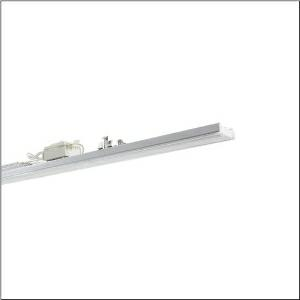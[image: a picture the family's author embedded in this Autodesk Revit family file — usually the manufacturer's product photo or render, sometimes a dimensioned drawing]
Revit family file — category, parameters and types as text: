
# Revit family: licross_r__21_recessed_mo_51te12vn48xg_da56
name_source: partatom
category: Lighting Fixtures
units: mm (PartAtom-declared; Revit-internal decimal feet)

## family parameters
Cut with Voids When Loaded = No
Host = Face
Light Source = No
Part Type = Normal
Room Calculation Point = No
Round Connector Dimension = Use Diameter
Shared = No

## types (1)
- --- (1 x LED, 8000 lm, 43.4 W, 4000K)
    Apparent Load = 43 VA
    CIE Flux Codes = 67 92 99 100 100
    Color Rendering = 80
    Color Temperature = 4000K
    Default Elevation = 1800 mm
    Description = Licross® 21 Recessed MO, luminaire insert, of sheet steel, galvanised, coil coated, white, length: 1.500mm, width: 66mm, height: 67mm, LED rated luminous flux: 8.000lm, light colour: 840, control gear: DALI 2, CLO, with plug, 5-pole, with phase selection, mains connection: 220..240V, AC, 50/60Hz, start of lifetime: 43W, end of service life: 48W, halogen-free wiring, primary optical cover: cover, of PMMA, light emission: direct distribution, primary light characteristic: symmetric, protection rating (complete): IP54, insulation class (complete): insulation class I (protective earthing), certification: CE, ENEC, VDE, UKCA, protection symbol: D if used in an environment with non-conductive dust loads with corresponding accessories, impact resistance: IK06, permissible ambient temperature for indoor applications: -25..+35°C, corresponds to IFS (International Featured Standards) requirements for safety and quality in the food industry, reducing of maximum allowable ambient temperature of 5°C with ceiling mounting, LABS conformity tested according to VDMA 24364:2018-05, packaging unit: 1 piece
    Height = 58 mm
    Lamp = 1 x LED
    Lamp Light Flux = 8000 lm
    Lamp Power = 43.4 W
    Lamp count = 1
    Length = 1500 mm
    Luminous efficacy = 184 lm/W
    Manufacturer = Siteco
    ModVariant = No
    Model = 51TE12VN48XG
    Mounting Place = Ceiling
    Mounting Type = Pendant
    Number of Poles = 1
    OnlyDefault = Yes
    Power Factor = 1
    Product Name = Licross® 21 Recessed MO
    Product group = luminaire insert
    ProductGroupID = 902
    Protection Class = Protection class I
    Protection Degree = IP 54
    RLX_Detail_Level = 1
    RLX_Emergency_Light_Flux = 0 lm
    RLX_Emergency_Type = 0
    RLX_Emergency_Type_DB = No
    RlxData = <blob elided: 24389 chars, md5=d5ee2fb9>
    Socket = socket
    Standby Power = 0 W
    System Light Flux = 8000 lm
    System Power = 43 W
    Type Comments = factory setting: luminous flux: 100 % | dim-lin: 254 | 289 mA
    Type Image = l_1296930.jpg
    URL = http://relux.com
    VarID = @adj_087388
    Voltage = 0 V
    Weight = 0.00 kg
    Width = 66 mm

## geometry (parser evidence)
native form markers: Blend x4, Sweep x12
no freeform markers — native parametric forms only
